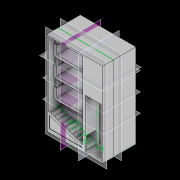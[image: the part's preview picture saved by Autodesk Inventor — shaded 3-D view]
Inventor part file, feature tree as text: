
AUTODESK INVENTOR PART (.ipt)
format: ipt  version: 2020 (Build 240168000, 168)  size: 1,778,688 bytes
history: native  units: mm
features: other x121, sketch x28, extrude x18, mirror x15, pattern_linear x14, plane x12, projected_geometry x8, hole x2, loft x2, chamfer x1
ambient origin geometry x8: Origin, YZ Plane, XZ Plane, XY Plane, X Axis, Y Axis, Z Axis, Center Point
bodies: Body1 (feature_tree), Body2 (feature_tree), Body3 (feature_tree), Body4 (feature_tree), Body5 (feature_tree), Body6 (feature_tree), Body7 (feature_tree), Body8 (feature_tree), Body9 (feature_tree), Body10 (feature_tree), Body11 (feature_tree), Body12 (feature_tree), Body13 (feature_tree), Body14 (feature_tree), Body15 (feature_tree), Body16 (feature_tree), Body17 (feature_tree), Body18 (feature_tree), Body19 (feature_tree), Body20 (feature_tree), Body21 (feature_tree), Body22 (feature_tree), Body23 (feature_tree), Body24 (feature_tree), Body25 (feature_tree), Body26 (feature_tree), Body27 (feature_tree), Body28 (feature_tree), Body29 (feature_tree), Body30 (feature_tree), Body31 (feature_tree), Body32 (feature_tree), Body33 (feature_tree), Body34 (feature_tree), Body35 (feature_tree), Body36 (feature_tree), Body37 (feature_tree), Body38 (feature_tree), Body39 (feature_tree), Body40 (feature_tree), Body41 (feature_tree), Body42 (feature_tree), Body43 (feature_tree), Body44 (feature_tree), Body45 (feature_tree)
feature tree (221):
  other  "實體1"
  extrude  "擠出1"  Depth=1200.0mm
  plane  "工作平面1"
  plane  "工作平面2"
  other  "分割1"
  plane  "工作平面3"
  extrude  "擠出3"  Depth=800.0mm
  plane  "工作平面6"
  plane  "工作平面7"
  extrude  "擠出4"  Depth=1820.0mm TaperAngle=0.0deg
  hole  "孔1"  [1 undecoded]
  pattern_linear  "矩形陣列1"  Spacing1=-80.0mm  [1 undecoded]
  pattern_linear  "矩形陣列2"  Spacing1=-30.0mm  [1 undecoded]
  pattern_linear  "矩形陣列3"  Count1=3  [1 undecoded]
  plane  "工作平面8"
  mirror  "鏡射1"
  mirror  "鏡射2"
  mirror  "鏡射3"
  extrude  "擠出5"  Depth=30.0mm
  plane  "工作平面9"
  other  "迴轉1"
  extrude  "擠出6"  Depth=30.0mm
  other  "迴轉2"
  plane  "工作平面10"
  extrude  "擠出7"  Depth=30.0mm
  loft  "斷面混成1"
  pattern_linear  "矩形陣列4"  Spacing1=-1230.0mm  [1 undecoded]
  pattern_linear  "矩形陣列5"  Count1=40 Spacing1=-345.0mm
  mirror  "鏡射4"
  mirror  "鏡射5"
  mirror  "鏡射6"
  pattern_linear  "矩形陣列6"  Count1=10  [1 undecoded]
  pattern_linear  "矩形陣列7"  Count1=2 Spacing1=0.0mm
  mirror  "鏡射7"
  mirror  "鏡射8"
  mirror  "鏡射9"
  sketch  "草圖13"
  extrude  "擠出8"  Depth=20.0mm
  extrude  "擠出9"  Depth=20.0mm
  extrude  "擠出10"  Depth=50.0mm
  extrude  "擠出11"  Depth=50.0mm
  other  "迴轉3"
  other  "迴轉4"
  plane  "工作平面11"
  extrude  "擠出12"  Depth=230.0mm
  loft  "斷面混成2"
  extrude  "擠出13"  Depth=20.0mm
  hole  "孔2"  [1 undecoded]
  pattern_linear  "矩形陣列8"  Spacing1=15.0mm  [1 undecoded]
  pattern_linear  "矩形陣列9"  Spacing1=11.0mm  [1 undecoded]
  pattern_linear  "矩形陣列10"  Spacing1=11.0mm  [1 undecoded]
  pattern_linear  "矩形陣列11"  Spacing1=11.0mm  [1 undecoded]
  mirror  "鏡射10"
  mirror  "鏡射11"
  mirror  "鏡射12"
  pattern_linear  "矩形陣列12"  Spacing1=11.0mm  [1 undecoded]
  pattern_linear  "矩形陣列13"  Spacing1=11.0mm  [1 undecoded]
  mirror  "鏡射13"
  mirror  "鏡射14"
  mirror  "鏡射15"
  extrude  "擠出14"  Depth=11.0mm
  plane  "工作平面12"
  other  "直接編輯1"
  other  "直接編輯2"
  other  "直接編輯3"
  other  "直接編輯4"
  other  "直接編輯5"
  other  "直接編輯6"
  sketch  "草圖26"
  extrude  "擠出15"  Depth=5.0mm TaperAngle=0.0deg
  chamfer  "倒角1"  Distance=10.0mm
  extrude  "擠出16"  Depth=15.0mm
  extrude  "擠出17"  Depth=2.5mm
  extrude  "擠出18"  TaperAngle=90.0deg  [1 undecoded]
  extrude  "擠出19"  Depth=10.0mm
  pattern_linear  "矩形陣列14"  Spacing1=1142.5mm  [1 undecoded]
  sketch  "草圖1"
  sketch  "草圖3"
  plane  "工作平面4"
  plane  "工作平面5"
  sketch  "草圖5"
  other  "實體4"
  sketch  "草圖6"
  other  "陣列 實體4:1"
  other  "實體5"
  other  "陣列 實體4:2"
  other  "實體6"
  other  "陣列 實體4:3"
  other  "實體7"
  other  "陣列 實體5:4"
  other  "實體8"
  other  "陣列 實體6:5"
  other  "實體9"
  sketch  "草圖7"
  other  "實體10"
  sketch  "草圖8"
  sketch  "草圖9"
  sketch  "草圖10"
  other  "實體11"
  sketch  "草圖11"
  projected_geometry  "投影迴路1"
  sketch  "草圖12"
  projected_geometry  "投影迴路2"
  other  "陣列 實體10:6"
  other  "實體12"
  other  "陣列 實體10:7"
  other  "實體13"
  other  "陣列 實體10:8"
  other  "實體14"
  other  "陣列 實體12:9"
  other  "實體15"
  other  "陣列 實體13:10"
  other  "實體16"
  other  "陣列 實體11:11"
  other  "實體17"
  other  "陣列 實體11:12"
  other  "實體18"
  other  "陣列 實體11:13"
  other  "實體19"
  other  "陣列 實體17:14"
  other  "實體20"
  other  "陣列 實體18:15"
  other  "實體21"
  sketch  "草圖14"
  projected_geometry  "投影迴路3"
  other  "實體22"
  sketch  "草圖15"
  sketch  "草圖16"
  sketch  "草圖17"
  projected_geometry  "投影迴路4"
  projected_geometry  "投影迴路5"
  projected_geometry  "投影迴路6"
  other  "實體23"
  sketch  "草圖18"
  sketch  "草圖19"
  other  "實體24"
  sketch  "草圖20"
  projected_geometry  "投影迴路7"
  sketch  "草圖21"
  sketch  "草圖22"
  sketch  "草圖23"
  other  "陣列 實體22:16"
  other  "實體25"
  other  "陣列 實體22:17"
  other  "實體26"
  other  "陣列 實體23:18"
  other  "實體27"
  other  "陣列 實體23:19"
  other  "實體28"
  other  "陣列 實體23:20"
  other  "實體29"
  other  "陣列 實體27:21"
  other  "實體30"
  other  "陣列 實體28:22"
  other  "實體31"
  other  "陣列 實體24:23"
  other  "實體32"
  other  "陣列 實體24:24"
  other  "實體33"
  other  "陣列 實體24:25"
  other  "實體34"
  other  "陣列 實體32:26"
  other  "實體35"
  other  "陣列 實體33:27"
  other  "實體36"
  sketch  "草圖24"
  sketch  "草圖27"
  sketch  "草圖28"
  sketch  "草圖29"
  sketch  "草圖30"
  projected_geometry  "投影迴路8"
  sketch  "草圖31"
  other  "實體37"
  other  "陣列 實體37:28"
  other  "實體38"
  other  "陣列 實體37:29"
  other  "實體39"
  other  "陣列 實體37:30"
  other  "實體40"
  other  "陣列 實體37:31"
  other  "實體41"
  other  "陣列 實體37:32"
  other  "實體42"
  other  "陣列 實體37:33"
  other  "實體43"
  other  "陣列 實體37:34"
  other  "實體44"
  other  "陣列 實體37:35"
  other  "實體45"
  other  "陣列 實體37:36"
  other  "實體46"
  other  "實體2"
  other  "實體3"
  other  "投影切割邊1"
  other  "投影切割邊2"
  other  "投影切割邊3"
  other  "投影切割邊4"
  other  "投影切割邊5"
  other  "投影切割邊6"
  other  "投影切割邊7"
  other  "投影切割邊8"
  other  "投影切割邊9"
  other  "投影切割邊10"
  other  "投影切割邊11"
  other  "投影切割邊12"
  other  "投影切割邊13"
  other  "投影切割邊14"
  other  "投影切割邊15"
  other  "投影切割邊16"
  other  "投影切割邊17"
  other  "移動1"
  other  "移動2"
  other  "移動3"
  other  "移動4"
  other  "移動5"
  other  "移動6"
  other  "投影切割邊18"
  other  "投影切割邊19"
  other  "投影切割邊20"
  other  "投影切割邊21"
  other  "投影切割邊22"
note: 15 required parameter values undecoded (feature->parameter linkage not recoverable at this tier; creation-order binding heuristic only, values carry confidence <= 0.55)
